# Revit family: Fluid-Storage_Water-Tank_Xerxes_Underground-Rainwater-Harvest-Stormwater-Detention
name_source: partatom
category: Generic Models
units: mm (PartAtom-declared; Revit-internal decimal feet)

## family parameters
Always vertical = No
Can host rebar = No
Classification Number = 23.65.20.11
Cut with Voids When Loaded = No
Maintain Annotation Orientation = No
Part Type = Normal
Room Calculation Point = No
Round Connector Dimension = Use Diameter
Shared = No
Work Plane-Based = Yes

## types (1)
- Fluid-Storage_Water-Tank_Xerxes_Underground-Rainwater-Harvest-Stormwater-Detention
    Actual Capacity Tank Section 1 = 0
    Assembly Code = G30
    Available LEED Credit = as Specified
    Brine Weight = 0
    Capacity = as Specified
    Construction Details = http://www.arcat.com
    Default Elevation = 0' - 0"
    Description = Xerxes Water Tank as Specified
    Diameter = 8' - 0"
    End Length = 3' - 7 3/4"
    Expected Lifespan (Years) = 0
    Keynote = 13200
    Maintenance Schedule (Months) = 0
    Manufacturer = Xerxes Corporation
    Manufacturer Fax = 952-887-1882
    Manufacturer Website = http://www.xerxes.com
    Model = As Specified
    Product Data = http://www.arcat.com
    Revision = R1_2015-07
    Rib Count = 18
    Rib Inset = 3' - 10"
    Ribs = Yes
    Sales Information = http://www.xerxes.com
    Small Size Resevoir Fitting = No
    SpecWizard = http://www.arcat.com
    Specification = http://www.arcat.com
    Standards Conformance = as Specified
    Tank Diameter Without Ribs = 7' - 8"
    URL = http://www.xerxes.com
    Unit Length = 31' - 6 1/2"
    Unit Weight = 0
    Unit Weight Notes = Unit Weight refers to empty tank only.
    Warranty Duration (Years) = 0
    ribcountcontrol = 18

## geometry (parser evidence)
native form markers: Sweep x8
no freeform markers — native parametric forms only
